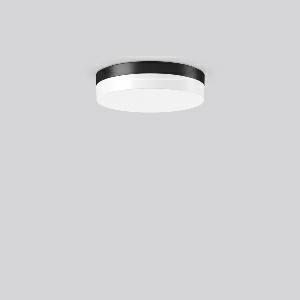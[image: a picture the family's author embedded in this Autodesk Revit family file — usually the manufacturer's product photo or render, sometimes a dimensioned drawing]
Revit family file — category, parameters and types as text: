
# Revit family: flat_slim_round_312630_0031_19_d9df
name_source: partatom
category: Lighting Fixtures
units: mm (PartAtom-declared; Revit-internal decimal feet)

## family parameters
Cut with Voids When Loaded = No
Host = Face
Light Source = No
Part Type = Normal
Room Calculation Point = No
Round Connector Dimension = Use Diameter
Shared = No

## types (1)
- MultiLumen 1 830 (1 x LED Modul 830, 1300 lm, 3000)
    Apparent Load = 11 VA
    CIE Flux Codes = 39 70 89 83 100
    Color Rendering = 80
    Color Temperature = 3000
    Default Elevation = 1800 mm
    Height = 70 mm
    Lamp = 1 x LED Modul 830
    Lamp Light Flux = 1300 lm
    Lamp count = 1
    Length = 300 mm
    Lifetime = 50000 h
    Luminous efficacy = 118 lm/W
    Manufacturer = RZB
    ModVariant = No
    Model = 312630.0031.19
    Mounting Place = Ceiling
    Mounting Type = Surface mounted
    Number of Poles = 1
    OnlyDefault = Yes
    Power Factor = 1
    Product Name = FLAT SLIM round
    Product group = Surface mounted ceiling and wall luminaires
    ProductGroupID = 305
    Protection Class = Protection class I
    Protection Degree = Degree of protection
    RLX_Detail_Level = 1
    RLX_Emergency_Light_Flux = 0 lm
    RLX_Emergency_Type = 0
    RLX_Emergency_Type_DB = No
    RlxData = <blob elided: 18009 chars, md5=1c16db60>
    Socket = socket
    Standby Power = 0 W
    System Light Flux = 1300 lm
    System Power = 11 W
    Type Comments = MultiLumen 1 830
    Type Image = 312629.0031.jpg
    URL = http://relux.com
    VarID = multilumen_1_830
    Voltage = 0 V
    Weight = 0.00 kg
    Width = 0 mm  [stored 0 ft]

note: [stored X ft] marks values corroborated as IEEE doubles in the binary element streams (Revit-internal decimal feet)

## geometry (parser evidence)
native form markers: Blend x4, Sweep x12
no freeform markers — native parametric forms only
